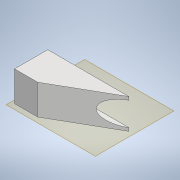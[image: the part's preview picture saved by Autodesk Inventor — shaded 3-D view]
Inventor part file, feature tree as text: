
AUTODESK INVENTOR PART (.ipt)
format: ipt  version: 2022.3 (Build 263350000, 350)  size: 125,952 bytes
history: native  units: mm
features: thicken_offset x4, extrude x3, sketch x3, other x2, plane x1, reference x1
ambient origin geometry x8: Origin, YZ Plane, XZ Plane, XY Plane, X Axis, Y Axis, Z Axis, Center Point
bodies: Solid1 (feature_tree)
feature tree (14):
  plane  "Work Plane1"
  extrude  "Extrusion1"  Depth=6.0mm
  extrude  "Extrusion2"  Depth=0.2mm
  thicken_offset  "Thicken1"
  thicken_offset  "Thicken2"
  extrude  "Extrusion3"  Depth=0.2mm
  thicken_offset  "Thicken3"
  thicken_offset  "Thicken4"
  sketch  "Sketch1"  dims[d0=8.0mm d1=0.0mm d2=6.0mm]
  reference  "Reference1"
  sketch  "Sketch2"  dims[d3=15.981mm d4=0.0mm d5=0.2mm]
  sketch  "Sketch3"  dims[d6=0.2mm d7=0.2mm d8=0.2mm d9=0.0mm d10=0.0mm d11=0.2mm d12=0.2mm d13=0.2mm d14=0.2mm]
  other  "v2.0.iam"
  other  "Base:1"
